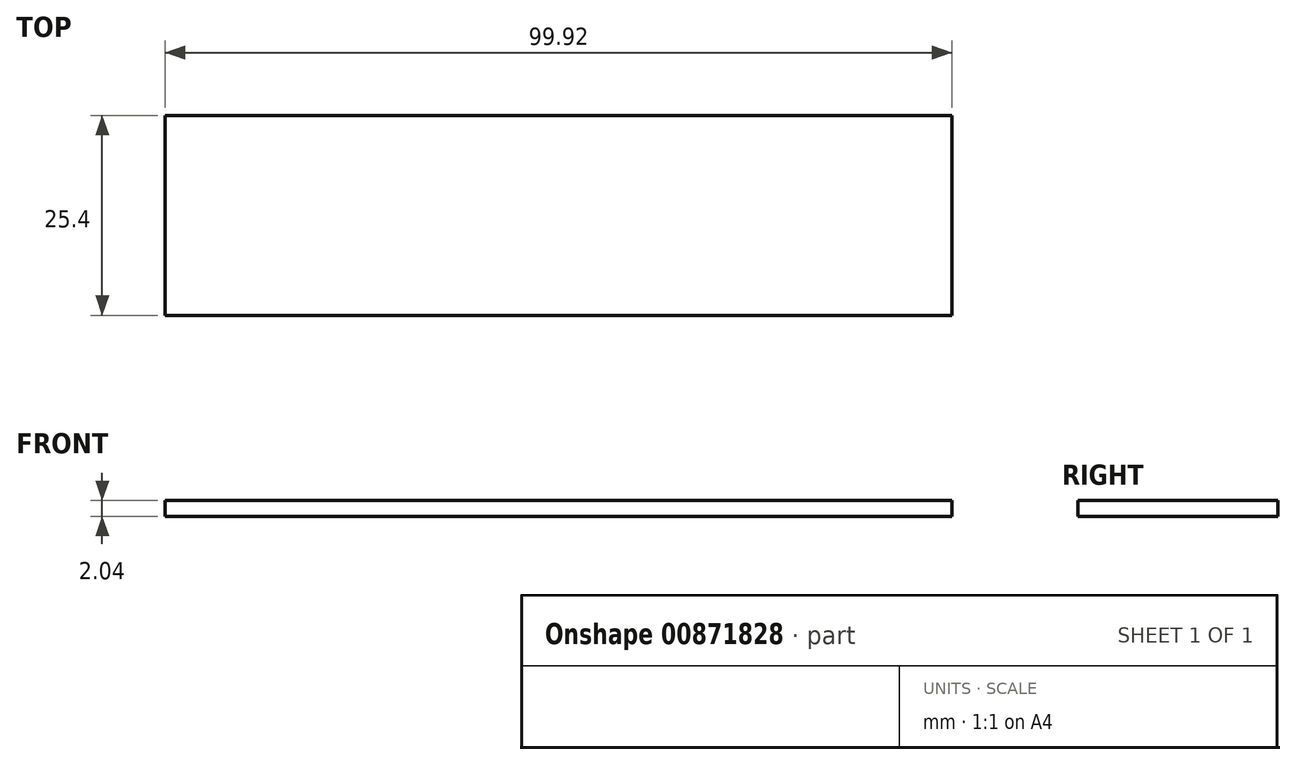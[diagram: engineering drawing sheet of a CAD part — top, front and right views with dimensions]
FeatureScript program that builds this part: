
annotation { "Feature Type Name" : "Feature", "Feature Type Description" : "" }
export const myFeature = defineFeature(function(context is Context, id is Id, definition is map)
    precondition{}
    {
        {
            var Q0;
            Q0=qCreatedBy(makeId("Front.planeOp"),FACE);
            var sketch = newSketch(context, id + "F0", { "sketchPlane" : qUnion([Q0])});
            skLineSegment(sketch, "E0.bottom", {"start": v(-53.46, 9.06) * mm, "end": v(46.46, 9.06) * mm});
            skLineSegment(sketch, "E0.top", {"start": v(-53.46, 7.02) * mm, "end": v(46.46, 7.02) * mm});
            skLineSegment(sketch, "E0.left", {"start": v(-53.46, 9.06) * mm, "end": v(-53.46, 7.02) * mm});
            skLineSegment(sketch, "E0.right", {"start": v(46.46, 9.06) * mm, "end": v(46.46, 7.02) * mm});
            skSolve(sketch);
        }
        {
            var Q0;
            Q0=makeQuery(id+"F0.imprint","IMPRINT",FACE,{"disambiguationData":[TD([[makeQuery(id+"F0.imprint","IMPRINT",EDGE,{"derivedFrom":sQuery(id+"F0.wireOp",EDGE,"E0.bottom")}),-1.0]])]});
            extrude(context, id + "F1", {"entities" : qUnion([Q0]), "depth" : 25.4 * mm, "offsetDistance" : 25.4 * mm});
        }
    });
